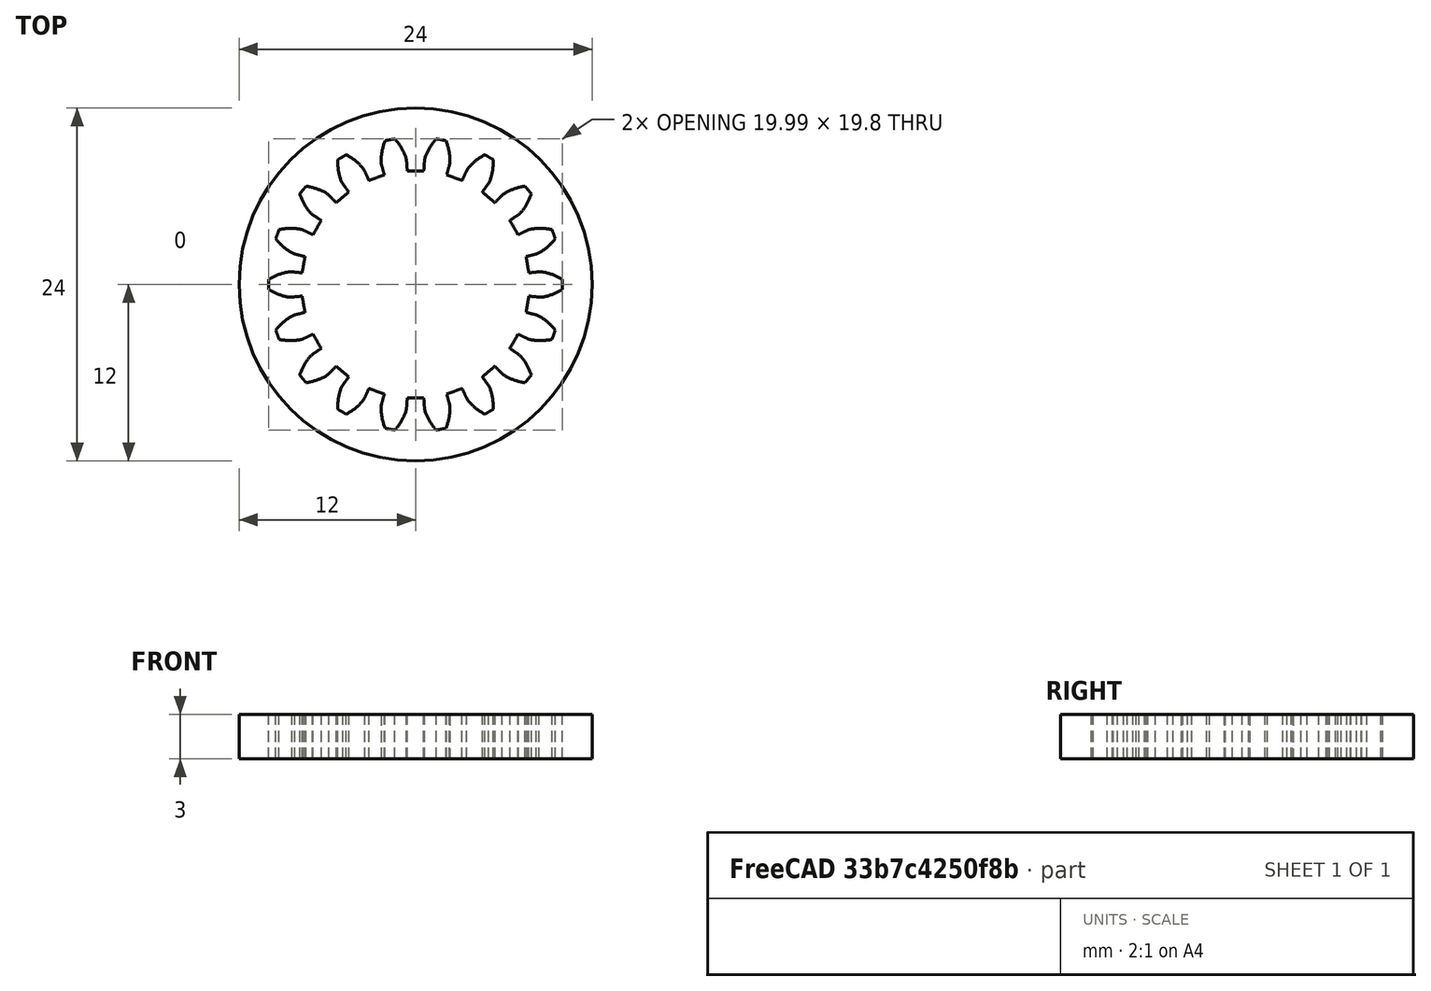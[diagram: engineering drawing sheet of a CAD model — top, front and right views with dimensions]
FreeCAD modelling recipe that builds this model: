
FCSTD DOCUMENT  (FreeCAD 0.19R24276 (Git))
Label: Gear_privod_perehodnik_to_GT2_test_3mm
License: All rights reserved
LicenseURL: http://en.wikipedia.org/wiki/All_rights_reserved
objects: Sketcher::SketchObject×1, PartDesign::FeaturePython×1, PartDesign::Pad×1, PartDesign::Body×1, Part::Cut×1
note: 6 computed .brp shape members not serialized (recipe doc carries the construction recipe); baked Part::Feature solids carry a one-line shape summary decoded from their .brp

FEATURE [Sketcher::SketchObject] Sketch
  FullyConstrained = true
  MapMode = 5
  Support = -> [XY_Plane]
  sketch-geometry (1):
    g0: Circle CenterX=0 CenterY=0 CenterZ=0 NormalX=0 NormalY=0 NormalZ=1 AngleXU=0 Radius=12
  constraints (2):
    c: Coincident(g0,g-1)
    c: Diameter(g0) = 24
FEATURE [PartDesign::FeaturePython] involutegear  # WARN: FeaturePython — macro-defined, semantics opaque (R4)
  AttacherType = Attacher::AttachEngine3D
  backlash = 0
  beta = 0
  clearance = 0.25
  da = 20
  df = 15.5
  double_helix = false
  dw = 18
  head = 0
  height = 3
  module = 1
  numpoints = 6
  pressure_angle = 20
  properties_from_tool = false
  reversed_backlash = false
  shift = 0
  simple = false
  teeth = 18
  transverse_pitch = 3.14159
  undercut = false
  version = 0.0.3
FEATURE [PartDesign::Pad] Pad
  BaseFeature = -> involutegear
  Direction = (1,1,1)
  Length = 3
  Length2 = 100
  Profile = -> Sketch
  Type = 0
FEATURE [PartDesign::Body] Body
  Group = -> [Sketch,involutegear,Pad]
  Origin = -> Origin
  Tip = -> Pad
FEATURE [Part::Cut] Cut
  Base = -> Pad
  Tool = -> involutegear
